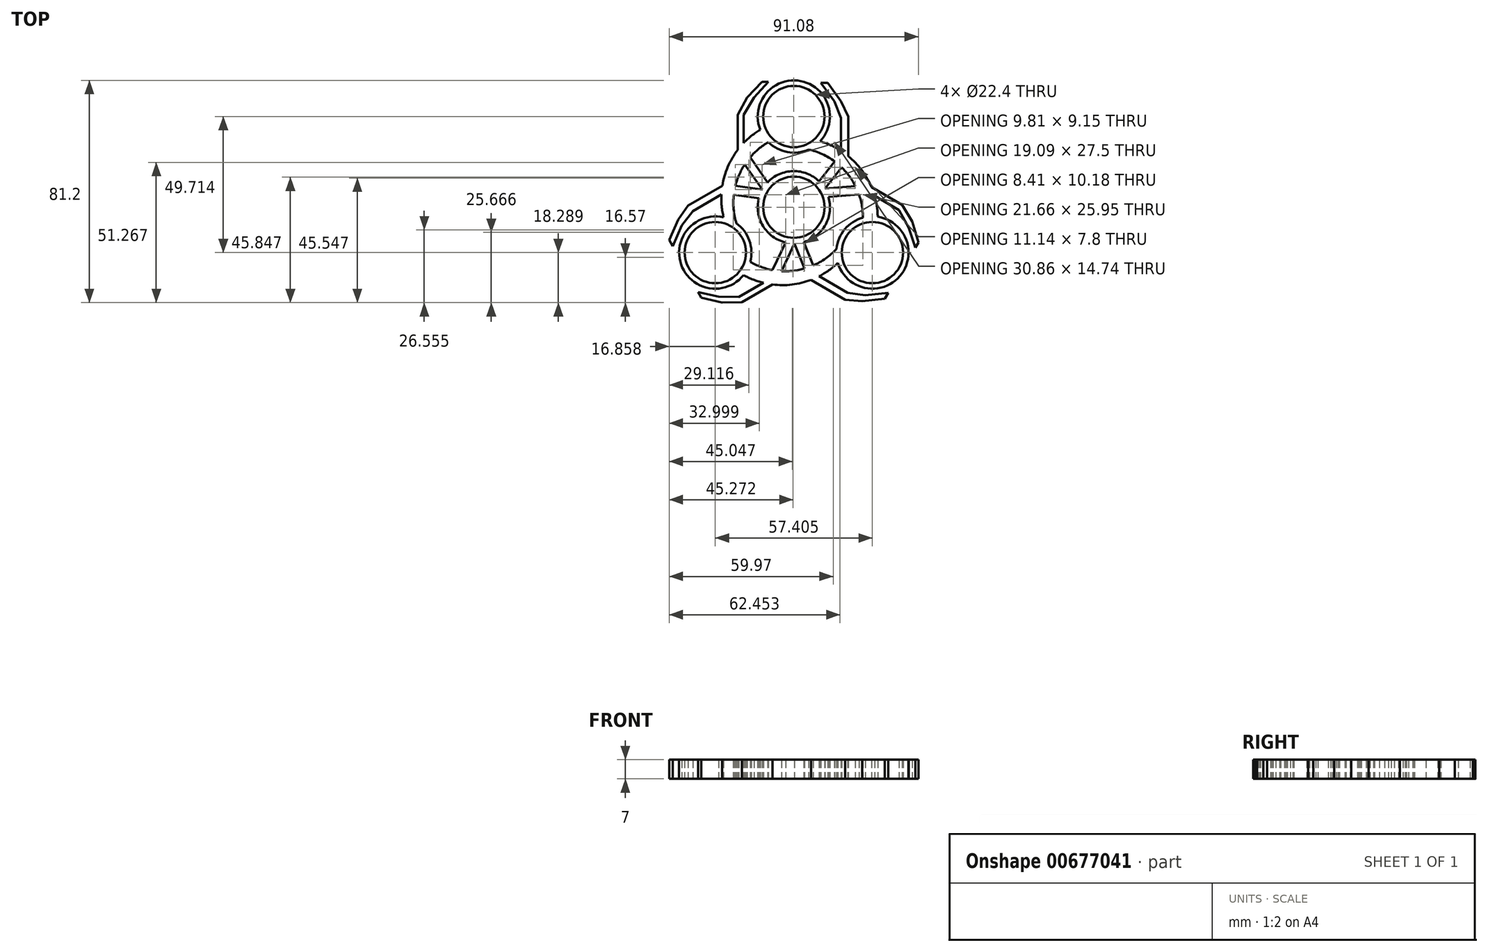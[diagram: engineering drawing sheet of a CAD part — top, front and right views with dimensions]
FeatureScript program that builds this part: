
annotation { "Feature Type Name" : "Feature", "Feature Type Description" : "" }
export const myFeature = defineFeature(function(context is Context, id is Id, definition is map)
    precondition{}
    {
        {
            var Q0;
            Q0=qCreatedBy(makeId("Top.planeOp"),FACE);
            var sketch = newSketch(context, id + "F0", { "sketchPlane" : qUnion([Q0])});
            skCircle(sketch, "E0", {"center": v(0, 0) * mm, "radius": 11.2 * mm});
            skArc(sketch, "E1", {"start": v(-12.8, 3.25) * mm, "mid": v(-11.28, -6.85) * mm, "end": v(-3.02, -12.85) * mm});
            skCircle(sketch, "E2", {"center": v(0, 33.14) * mm, "radius": 11.2 * mm});
            skCircle(sketch, "E3.1.0", {"center": v(-28.7, -16.57) * mm, "radius": 11.2 * mm});
            skArc(sketch, "E3.1.1", {"start": v(-15.94, -19.94) * mm, "mid": v(-40.5, -10.65) * mm, "end": v(-18.37, -24.78) * mm});
            skCircle(sketch, "E3.2.0", {"center": v(28.7, -16.57) * mm, "radius": 11.2 * mm});
            skArc(sketch, "E3.2.1", {"start": v(25.24, -3.83) * mm, "mid": v(18.63, -8.04) * mm, "end": v(15.57, -15.25) * mm});
            skPoint(sketch, "E4.center", {"position": v(0, -0.01) * mm});
            skLineSegment(sketch, "E5", {"start": v(-20.54, 19.21) * mm, "end": v(-20.54, 33.77) * mm});
            skLineSegment(sketch, "E6", {"start": v(-20.54, 33.77) * mm, "end": v(-17.1, 40.1) * mm});
            skLineSegment(sketch, "E7", {"start": v(-17.1, 40.1) * mm, "end": v(-11.64, 45.84) * mm});
            skLineSegment(sketch, "E8", {"start": v(-18.37, 21.82) * mm, "end": v(-18.37, 33.77) * mm});
            skLineSegment(sketch, "E9", {"start": v(-18.37, 33.77) * mm, "end": v(-14.53, 40.1) * mm});
            skLineSegment(sketch, "E10", {"start": v(-14.53, 40.1) * mm, "end": v(-9.38, 45.84) * mm});
            skLineSegment(sketch, "E11", {"start": v(-11.64, 45.84) * mm, "end": v(-9.38, 45.84) * mm});
            skArc(sketch, "E12", {"start": v(-9.3, 23.78) * mm, "mid": v(-2.36, 20.15) * mm, "end": v(5.42, 21.1) * mm});
            skLineSegment(sketch, "E13.1.0", {"start": v(-20.06, -32.8) * mm, "end": v(-27.46, -32.63) * mm});
            skLineSegment(sketch, "E13.1.1", {"start": v(-27.46, -32.63) * mm, "end": v(-35.01, -31.04) * mm});
            skLineSegment(sketch, "E13.1.2", {"start": v(-26.17, -34.86) * mm, "end": v(-33.88, -33) * mm});
            skLineSegment(sketch, "E13.1.3", {"start": v(-33.88, -33) * mm, "end": v(-35.01, -31.04) * mm});
            skLineSegment(sketch, "E13.1.4", {"start": v(-18.98, -34.67) * mm, "end": v(-26.17, -34.86) * mm});
            skLineSegment(sketch, "E13.1.5", {"start": v(-9.71, -26.81) * mm, "end": v(-20.06, -32.8) * mm});
            skLineSegment(sketch, "E13.1.6", {"start": v(-6.37, -27.4) * mm, "end": v(-18.98, -34.67) * mm});
            skLineSegment(sketch, "E13.2.0", {"start": v(38.43, -0.98) * mm, "end": v(41.99, -7.46) * mm});
            skLineSegment(sketch, "E13.2.1", {"start": v(41.99, -7.46) * mm, "end": v(44.39, -14.8) * mm});
            skLineSegment(sketch, "E13.2.2", {"start": v(43.27, -5.24) * mm, "end": v(45.52, -12.84) * mm});
            skLineSegment(sketch, "E13.2.3", {"start": v(45.52, -12.84) * mm, "end": v(44.39, -14.8) * mm});
            skLineSegment(sketch, "E13.2.4", {"start": v(39.52, 0.9) * mm, "end": v(43.27, -5.24) * mm});
            skLineSegment(sketch, "E13.2.5", {"start": v(28.08, 5) * mm, "end": v(38.43, -0.98) * mm});
            skLineSegment(sketch, "E13.2.6", {"start": v(26.9, 8.18) * mm, "end": v(39.52, 0.9) * mm});
            skLineSegment(sketch, "E14", {"start": v(19.87, 17.69) * mm, "end": v(19.87, 33.12) * mm});
            skLineSegment(sketch, "E15", {"start": v(17.23, 19.68) * mm, "end": v(17.23, 32.58) * mm});
            skLineSegment(sketch, "E16", {"start": v(17.23, 32.58) * mm, "end": v(14.78, 38.75) * mm});
            skLineSegment(sketch, "E17", {"start": v(19.87, 33.12) * mm, "end": v(17.23, 38.75) * mm});
            skPoint(sketch, "E17.endSnap0", {"position": v(17.23, 26.13) * mm});
            skLineSegment(sketch, "E18", {"start": v(17.23, 38.75) * mm, "end": v(12.38, 45.46) * mm});
            skLineSegment(sketch, "E19", {"start": v(14.78, 38.75) * mm, "end": v(9.8, 45.46) * mm});
            skLineSegment(sketch, "E20", {"start": v(9.8, 45.46) * mm, "end": v(12.38, 45.46) * mm});
            skLineSegment(sketch, "E21.1.0", {"start": v(-25.25, 8.36) * mm, "end": v(-38.61, 0.65) * mm});
            skLineSegment(sketch, "E21.1.1", {"start": v(-25.66, 5.08) * mm, "end": v(-36.83, -1.36) * mm});
            skLineSegment(sketch, "E21.1.2", {"start": v(-38.61, 0.65) * mm, "end": v(-42.18, -4.45) * mm});
            skLineSegment(sketch, "E21.1.3", {"start": v(-36.83, -1.36) * mm, "end": v(-40.95, -6.58) * mm});
            skLineSegment(sketch, "E21.1.4", {"start": v(-42.18, -4.45) * mm, "end": v(-45.56, -12) * mm});
            skLineSegment(sketch, "E21.1.5", {"start": v(-40.95, -6.58) * mm, "end": v(-44.27, -14.24) * mm});
            skLineSegment(sketch, "E21.1.6", {"start": v(-44.27, -14.24) * mm, "end": v(-45.56, -12) * mm});
            skLineSegment(sketch, "E21.2.0", {"start": v(5.38, -26.05) * mm, "end": v(18.75, -33.76) * mm});
            skLineSegment(sketch, "E21.2.1", {"start": v(8.43, -24.77) * mm, "end": v(19.6, -31.21) * mm});
            skLineSegment(sketch, "E21.2.2", {"start": v(18.75, -33.76) * mm, "end": v(24.94, -34.3) * mm});
            skLineSegment(sketch, "E21.2.3", {"start": v(19.6, -31.21) * mm, "end": v(26.17, -32.17) * mm});
            skLineSegment(sketch, "E21.2.4", {"start": v(24.94, -34.3) * mm, "end": v(33.18, -33.45) * mm});
            skLineSegment(sketch, "E21.2.5", {"start": v(26.17, -32.17) * mm, "end": v(34.47, -31.22) * mm});
            skLineSegment(sketch, "E21.2.6", {"start": v(34.47, -31.22) * mm, "end": v(33.18, -33.45) * mm});
            skLineSegment(sketch, "E22", {"start": v(17.23, 19.68) * mm, "end": v(9.21, 9.45) * mm});
            skLineSegment(sketch, "E23", {"start": v(19.87, 17.69) * mm, "end": v(11.32, 6.79) * mm});
            skLineSegment(sketch, "E24.1.0", {"start": v(-25.66, 5.08) * mm, "end": v(-12.8, 3.25) * mm});
            skLineSegment(sketch, "E24.1.1", {"start": v(-25.25, 8.36) * mm, "end": v(-11.54, 6.4) * mm});
            skLineSegment(sketch, "E24.2.0", {"start": v(8.43, -24.77) * mm, "end": v(3.58, -12.7) * mm});
            skLineSegment(sketch, "E24.2.1", {"start": v(5.38, -26.05) * mm, "end": v(0.22, -13.2) * mm});
            skLineSegment(sketch, "E25", {"start": v(-20.54, 19.21) * mm, "end": v(-11.54, 6.4) * mm});
            skLineSegment(sketch, "E26", {"start": v(-18.37, 21.82) * mm, "end": v(-9.62, 9.04) * mm});
            skLineSegment(sketch, "E27.1.0", {"start": v(-9.71, -26.81) * mm, "end": v(-3.02, -12.85) * mm});
            skLineSegment(sketch, "E27.1.1", {"start": v(-6.37, -27.4) * mm, "end": v(0.22, -13.2) * mm});
            skLineSegment(sketch, "E27.2.0", {"start": v(28.08, 5) * mm, "end": v(12.64, 3.81) * mm});
            skLineSegment(sketch, "E27.2.1", {"start": v(26.9, 8.18) * mm, "end": v(11.32, 6.79) * mm});
            skArc(sketch, "E28", {"start": v(-12.28, 28.3) * mm, "mid": v(-15.48, 26.08) * mm, "end": v(-18.37, 23.45) * mm});
            skArc(sketch, "E29", {"start": v(-9.3, 23.78) * mm, "mid": v(-12.86, 21.3) * mm, "end": v(-15.94, 18.27) * mm});
            skArc(sketch, "E30.1.0", {"start": v(-15.94, -19.94) * mm, "mid": v(-12.03, -21.79) * mm, "end": v(-7.86, -22.94) * mm});
            skArc(sketch, "E30.1.1", {"start": v(-18.37, -24.78) * mm, "mid": v(-14.84, -26.45) * mm, "end": v(-11.12, -27.63) * mm});
            skArc(sketch, "E30.2.0", {"start": v(25.24, -3.83) * mm, "mid": v(24.88, 0.48) * mm, "end": v(23.8, 4.67) * mm});
            skArc(sketch, "E30.2.1", {"start": v(30.65, -3.52) * mm, "mid": v(30.33, 0.37) * mm, "end": v(29.49, 4.18) * mm});
            skArc(sketch, "E31.trimOffspring", {"start": v(-20.54, 20.9) * mm, "mid": v(-24.13, 14.72) * mm, "end": v(-26.12, 7.86) * mm});
            skArc(sketch, "E32.trimOffspring", {"start": v(-17.97, 15.56) * mm, "mid": v(-19.98, 11.83) * mm, "end": v(-21.35, 7.8) * mm});
            skArc(sketch, "E33.trimOffspring", {"start": v(9.6, 24.09) * mm, "mid": v(2.5, 46.1) * mm, "end": v(-12.28, 28.3) * mm});
            skArc(sketch, "E34.trimOffspring", {"start": v(16.06, -20.36) * mm, "mid": v(38.68, -25.21) * mm, "end": v(30.65, -3.52) * mm});
            skArc(sketch, "E35.trimOffspring", {"start": v(-26.46, 4.62) * mm, "mid": v(-26.36, 0.42) * mm, "end": v(-25.66, -3.73) * mm});
            skArc(sketch, "E36.trimOffspring", {"start": v(-21.94, 4.56) * mm, "mid": v(-22, -0.7) * mm, "end": v(-20.99, -5.86) * mm});
            skArc(sketch, "E37.trimOffspring", {"start": v(14.91, 16.72) * mm, "mid": v(10.4, 19.4) * mm, "end": v(5.42, 21.1) * mm});
            skArc(sketch, "E38.trimOffspring", {"start": v(17.23, 20.6) * mm, "mid": v(13.54, 22.62) * mm, "end": v(9.6, 24.09) * mm});
            skArc(sketch, "E39.trimOffspring", {"start": v(22.47, 7.78) * mm, "mid": v(20.23, 11.4) * mm, "end": v(17.43, 14.59) * mm});
            skArc(sketch, "E40.trimOffspring", {"start": v(28.37, 7.34) * mm, "mid": v(24.82, 13.54) * mm, "end": v(19.87, 18.7) * mm});
            skArc(sketch, "E41.trimOffspring", {"start": v(9.23, -25.23) * mm, "mid": v(12.82, -23.04) * mm, "end": v(16.06, -20.36) * mm});
            skArc(sketch, "E42.trimOffspring", {"start": v(7.02, -21.28) * mm, "mid": v(11.6, -18.7) * mm, "end": v(15.57, -15.25) * mm});
            skArc(sketch, "E43.trimOffspring", {"start": v(-4.5, -23.35) * mm, "mid": v(-0.25, -23.22) * mm, "end": v(3.91, -22.4) * mm});
            skArc(sketch, "E44.trimOffspring", {"start": v(-7.83, -28.24) * mm, "mid": v(-0.68, -28.26) * mm, "end": v(6.26, -26.55) * mm});
            skArc(sketch, "E45.trimOffspring", {"start": v(3.58, -12.7) * mm, "mid": v(11.57, -6.35) * mm, "end": v(12.64, 3.81) * mm});
            skArc(sketch, "E46.trimOffspring", {"start": v(9.21, 9.45) * mm, "mid": v(-0.3, 13.2) * mm, "end": v(-9.62, 9.04) * mm});
            skSolve(sketch);
        }
        {
            var Q0;
            Q0=makeQuery(id+"F0.imprint","IMPRINT",FACE,{"disambiguationData":[TD([[makeQuery(id+"F0.imprint","IMPRINT",EDGE,{"derivedFrom":sQuery(id+"F0.wireOp",EDGE,"E0")}),-1.0]])]});
            var Q1;
            Q1=makeQuery(id+"F0.imprint","IMPRINT",FACE,{"disambiguationData":[TD([[makeQuery(id+"F0.imprint","IMPRINT",EDGE,{"derivedFrom":sQuery(id+"F0.wireOp",EDGE,"E3.1.0")}),-1.0]])]});
            var Q2;
            {var subQ3=sQuery(id+"F0.wireOp",EDGE,"E43.trimOffspring");Q2=makeQuery(id+"F0.imprint","IMPRINT",FACE,{"disambiguationData":[TD([[makeQuery(id+"F0.imprint","IMPRINT",EDGE,{"derivedFrom":subQ3}),-1.0]])]});}
            var Q3;
            Q3=makeQuery(id+"F0.imprint","IMPRINT",FACE,{"disambiguationData":[TD([[makeQuery(id+"F0.imprint","IMPRINT",EDGE,{"derivedFrom":sQuery(id+"F0.wireOp",EDGE,"E3.2.0")}),-1.0]])]});
            var Q4;
            {var subQ3=sQuery(id+"F0.wireOp",EDGE,"E39.trimOffspring");Q4=makeQuery(id+"F0.imprint","IMPRINT",FACE,{"disambiguationData":[TD([[makeQuery(id+"F0.imprint","IMPRINT",EDGE,{"derivedFrom":subQ3}),-1.0]])]});}
            var Q5;
            Q5=makeQuery(id+"F0.imprint","IMPRINT",FACE,{"disambiguationData":[TD([[makeQuery(id+"F0.imprint","IMPRINT",EDGE,{"derivedFrom":sQuery(id+"F0.wireOp",EDGE,"E2")}),-1.0]])]});
            var Q6;
            {var subQ7=sQuery(id+"F0.wireOp",EDGE,"E31.trimOffspring");Q6=makeQuery(id+"F0.imprint","IMPRINT",FACE,{"disambiguationData":[TD([[makeQuery(id+"F0.imprint","IMPRINT",EDGE,{"derivedFrom":subQ7}),1.0]])]});}
            var Q7;
            {var subQ0=sQuery(id+"F0.wireOp",EDGE,"E35.trimOffspring");Q7=makeQuery(id+"F0.imprint","IMPRINT",FACE,{"disambiguationData":[TD([[makeQuery(id+"F0.imprint","IMPRINT",EDGE,{"derivedFrom":subQ0}),1.0]])]});}
            extrude(context, id + "F1", {"entities" : qUnion([Q0, Q1, Q2, Q3, Q4, Q5, Q6, Q7]), "depth" : 7 * mm, "offsetDistance" : 25 * mm});
        }
    });
